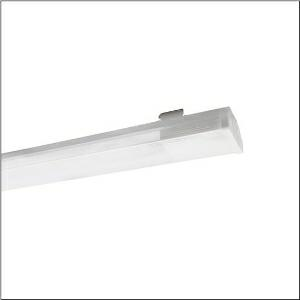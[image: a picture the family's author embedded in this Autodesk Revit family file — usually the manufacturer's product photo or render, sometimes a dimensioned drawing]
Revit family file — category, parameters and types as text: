
# Revit family: modario_r__31_gen_2_53bm813du4l3d2_6b72
name_source: partatom
category: Lighting Fixtures
units: mm (PartAtom-declared; Revit-internal decimal feet)

## family parameters
Cut with Voids When Loaded = No
Host = Face
Light Source = No
Part Type = Normal
Room Calculation Point = No
Round Connector Dimension = Use Diameter
Shared = No

## types (1)
- --- (1 x LED, 23060 lm, 128.4 W, 4000K)
    Apparent Load = 128 VA
    CIE Flux Codes = 62 83 95 93 100
    Color Rendering = 80
    Color Temperature = 4000K
    Default Elevation = 1800 mm
    Description = Modario® 31 Gen.2, luminaire insert, of sheet steel, coil coated, white, length: 2.392mm, width: 81mm, height: 82mm, 8x system unit, system units: 299mm, LED rated luminous flux: 23.060lm, light colour: 840, control gear: DALI 2, control gear: ECG DALI, with plug, 5-pole, with phase selection, mains connection: 220..240V, AC, 50/60Hz, rated input power: 128W, through-wiring accessed according to module size, primary optical cover: cover, of PMMA, light emission: direct distribution, primary light characteristic: symmetric, protection rating (complete): IP20, protection rating (LED compartment): IP50, insulation class (complete): insulation class I (protective earthing), certification: CE, ENEC, VDE, UKCA, impact resistance: IK03, permissible ambient temperature for indoor applications: -40..+35°C, corresponds to IFS (International Featured Standards) requirements for safety and quality in the food industry, reducing of maximum allowable ambient temperature of 5°C with ceiling mounting, packaging unit: 1 piece
    Height = 92 mm
    Lamp = 1 x LED
    Lamp Light Flux = 23060 lm
    Lamp Power = 128.4 W
    Lamp count = 1
    Length = 2392 mm
    Luminous efficacy = 180 lm/W
    Manufacturer = Siteco
    ModVariant = No
    Model = 53BM813DU4L3D2
    Mounting Place = Ceiling
    Mounting Type = Pendant
    Number of Poles = 1
    OnlyDefault = Yes
    Power Factor = 1
    Product Name = Modario® 31 Gen.2
    Product group = luminaire insert | ceiling pendant
    ProductGroupID = 902
    Protection Class = Protection class I
    Protection Degree = IP 20
    RLX_Detail_Level = 1
    RLX_Emergency_Light_Flux = 0 lm
    RLX_Emergency_Type = 0
    RLX_Emergency_Type_DB = No
    RlxData = <blob elided: 38681 chars, md5=f9a0bec4>
    Socket = socket
    Standby Power = 0 W
    System Light Flux = 23061 lm
    System Power = 128 W
    Type Comments = factory setting: luminous flux: 100 % | dim-lin: 254 | 594 mA
    Type Image = l_1341883.jpg
    URL = http://relux.com
    VarID = @adj_064881
    Voltage = 0 V
    Weight = 0.00 kg
    Width = 81 mm

## geometry (parser evidence)
native form markers: Blend x4, Sweep x10
no freeform markers — native parametric forms only
